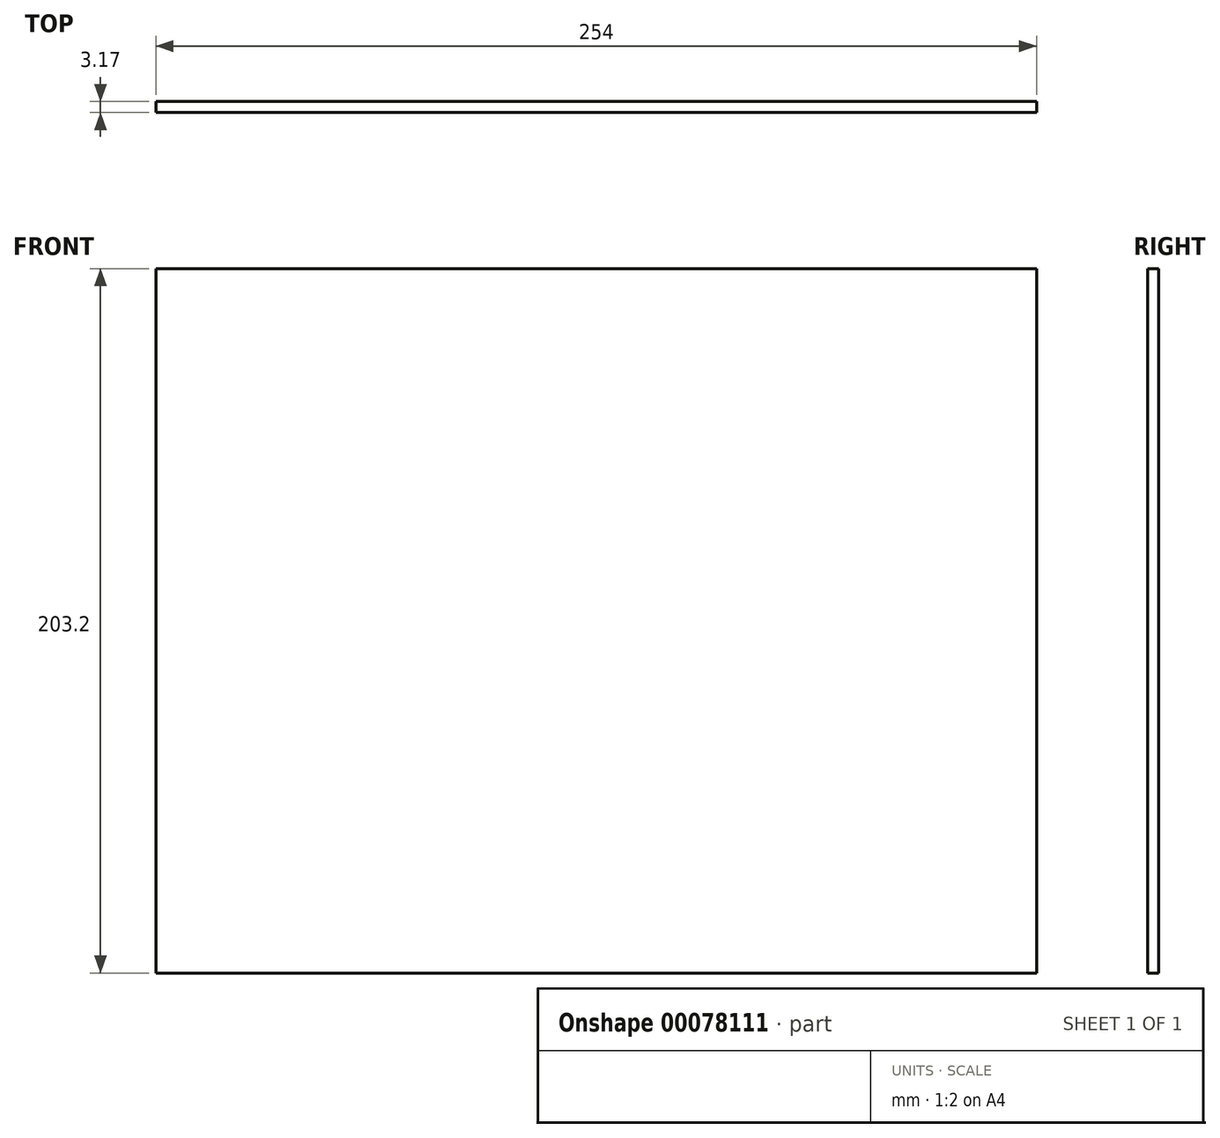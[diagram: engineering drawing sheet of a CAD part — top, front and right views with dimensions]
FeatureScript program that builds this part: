
annotation { "Feature Type Name" : "Feature", "Feature Type Description" : "" }
export const myFeature = defineFeature(function(context is Context, id is Id, definition is map)
    precondition{}
    {
        {
            var Q0;
            Q0=qCreatedBy(makeId("Front.planeOp"),FACE);
            var sketch = newSketch(context, id + "F0", { "sketchPlane" : qUnion([Q0])});
            skLineSegment(sketch, "E0.bottom", {"start": v(-124.29, 113.13) * mm, "end": v(129.71, 113.13) * mm});
            skLineSegment(sketch, "E0.top", {"start": v(-124.29, -90.07) * mm, "end": v(129.71, -90.07) * mm});
            skLineSegment(sketch, "E0.left", {"start": v(-124.29, 113.13) * mm, "end": v(-124.29, -90.07) * mm});
            skLineSegment(sketch, "E0.right", {"start": v(129.71, 113.13) * mm, "end": v(129.71, -90.07) * mm});
            skSolve(sketch);
        }
        {
            var Q0;
            Q0=makeQuery(id+"F0.imprint","IMPRINT",FACE,{"disambiguationData":[TD([[makeQuery(id+"F0.imprint","IMPRINT",EDGE,{"derivedFrom":sQuery(id+"F0.wireOp",EDGE,"E0.bottom")}),-1.0]])]});
            extrude(context, id + "F1", {"entities" : qUnion([Q0]), "depth" : 3.17 * mm});
        }
    });
